# Revit family: HDPR48_Revit
name_source: partatom
category: Specialty Equipment
revit_build: Autodesk Revit MEP 2014 (Build: 20130308_1515(x64)
units: mm (PartAtom-declared; Revit-internal decimal feet)

## types (1)
- HDPR48
    Adjustment = Stainless Steel
    BAKE ELEMENT = 3,000W - 8 PASS (LG) 2,100W (SM)
    BROIL ELEMENT = 3,500W - 8 PASS (LG) 2,500W (SM)
    Burner = Plastic-Black
    CAVITY = BLACK ENAMEL COATING
    CENTER FRONT (BTU) = 15,000 STACK DUAL (SIMMER)
    CENTER REAR (BTU) = 15,000 STACK DUAL (SIMMER)
    CHILD LOCK = YES
    CIRCUIT BREAKER (A) = 50 AMP
    CLEANING TYPE = SELF CLEAN GREENCLEAN™
    CLOCK = YES
    CONTROL METHOD = LED GLASS TOUCH CONTROL
    CONVECTION ELEMENT = 2,200W (LG) 2,200W (SM)
    COOKING MODES = PURE CONVECTION™ CONVECTION BAKE CONVECTION BROIL CONVECTION ROAST BAKE BROIL
    DEHYDRATE = YES (BOTH)
    DELAY START = YES
    Depth = 24"
    Description = 48-INCH PRO DUAL-FUEL RANGE HERIT AGE COLLECTION
    Door = Stainless Steel
    ENERGY SOURCE = GAS AND ELECTRICAL
    FREQUENCY (HZ) = 60 HZ
    GAS TYPES = NATURAL GAS NATURAL GAS (HIGH ALTITUDE) LIQUID PROPANE LIQUID PROPANE (HIGH ALTITUDE)
    Gas Burner = Stainless Steel
    Glide = Plastic-Black
    HIGHLIGHTING COLOR = WHITE
    Handle = Stainless Steel
    Height = 37 1/2"
    ILLUMINA™ BURNER KNOBS = YES
    KEEP WARM = YES (BOTH)
    KITCHEN TIMER = YES 1 PER OVEN
    LED (WHITE) = YES
    LEFT FRONT (BTU) = 18,000 STACK DUAL (SIMMER/SEAR)
    LEFT REAR (BTU) = 15,000 STACK DUAL (SIMMER)
    LIGHTING = LED & HALOGEN
    Manufacturer = Dacor
    Model = HDPR48
    NUMBER OF KNOBS = 6 KNOBS
    OVEN CAPACITY (CUBIC FEET) = 5.2 (LG OVEN) / 2.8 (SM OVEN)
    PERMA-FLAME™ (AUTO RE-IGNITION) = YES
    PROOF = YES (BOTH)
    RACK POSITIONS = 6 (LG) / 6 (SM)
    RIGHT FRONT (BTU) = 18,000 DUAL (SIMMER/SEAR)
    RIGHT REAR (BTU) = 15,000 STACK DUAL (SIMMER)
    SABBATH = YES (BOTH)
    SEALED BURNERS = YES
    SOUND ON/OFF = YES
    Support = Glass
    TEMPERATURE (F/C) = YES
    TEMPERATURE PROBE = YES (LG OVEN)
    TIME OF DAY (12 HR/24 HR) = YES
    TOTAL NUMBER OF COOKTOP BURNERS = 6 DUAL STACK BRASS BURNERS
    TYPE OF GRATE = CONTINUOUS CAST IRON
    Unit = Stainless Steel
    VOLTS (V) = 240 V
    Width = 48"

## geometry (parser evidence)
native form markers: Blend x4, Sweep x3
no freeform markers — native parametric forms only
